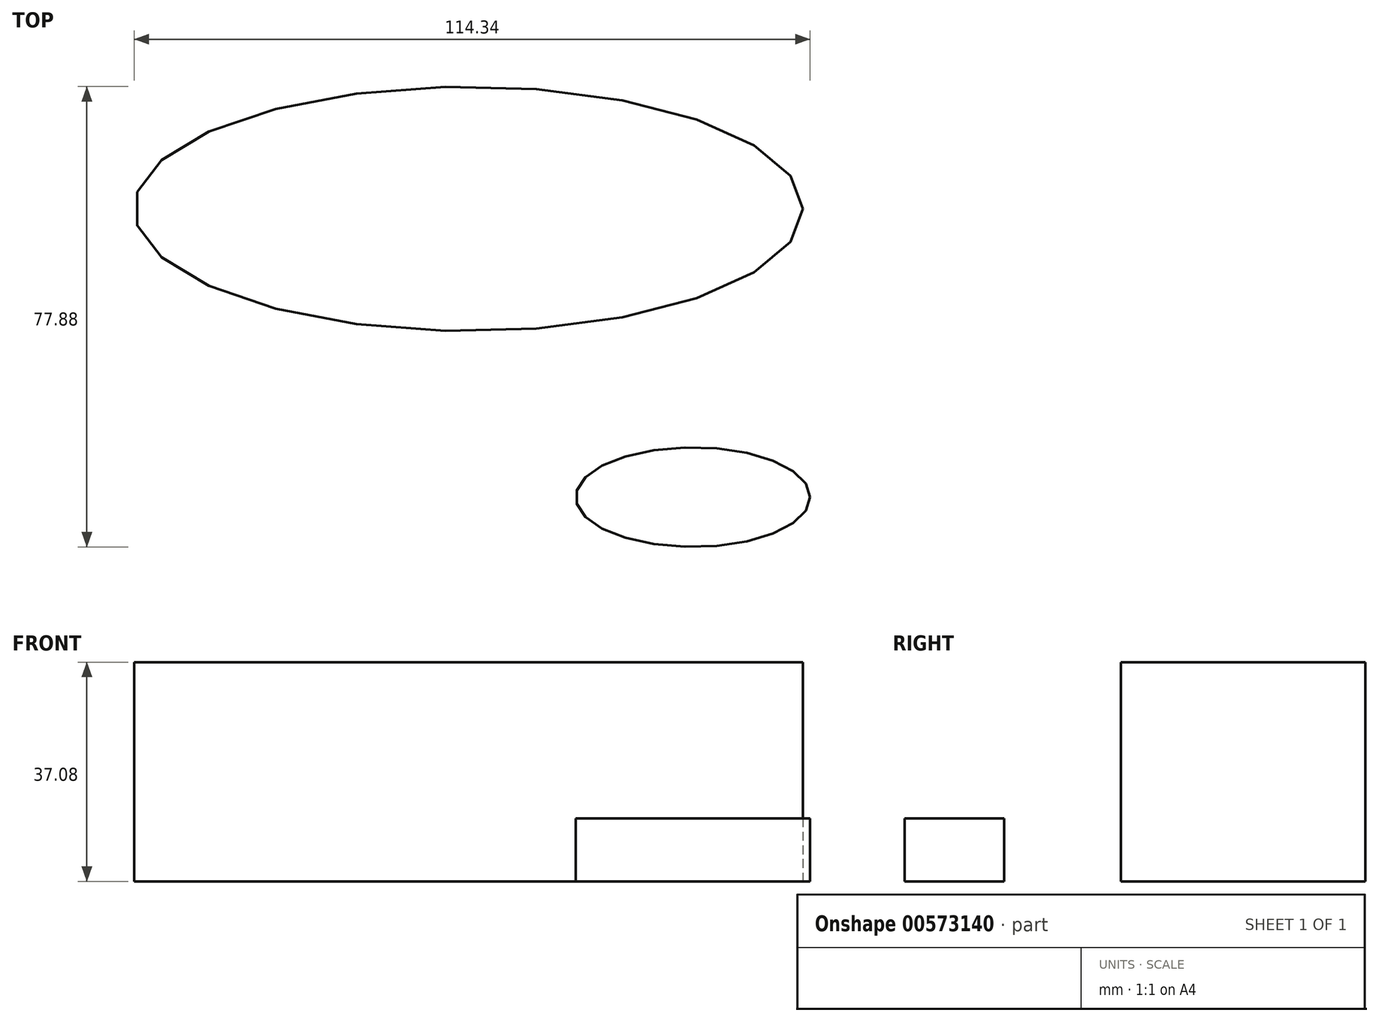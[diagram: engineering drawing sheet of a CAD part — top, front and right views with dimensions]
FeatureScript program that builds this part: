
annotation { "Feature Type Name" : "Feature", "Feature Type Description" : "" }
export const myFeature = defineFeature(function(context is Context, id is Id, definition is map)
    precondition{}
    {
        {
            var Q0;
            Q0=qCreatedBy(makeId("Top.planeOp"),FACE);
            var sketch = newSketch(context, id + "F0", { "sketchPlane" : qUnion([Q0])});
            skEllipse(sketch, "E0", {"center": v(-7.29, 11.51) * mm, "majorRadius": 56.55 * mm, "minorRadius": 20.67 * mm, "majorAxis": v(1, 0)});
            skSolve(sketch);
        }
        {
            var Q0;
            Q0 = qSketchRegion(id + "F0", true);
            extrude(context, id + "F1", {"entities" : qUnion([Q0]), "depth" : 37.08 * mm, "offsetDistance" : 25.4 * mm});
        }
        {
            var Q0;
            Q0=qCreatedBy(makeId("Top.planeOp"),FACE);
            var sketch = newSketch(context, id + "F2", { "sketchPlane" : qUnion([Q0])});
            skEllipse(sketch, "E1", {"center": v(30.68, -37.27) * mm, "majorRadius": 19.83 * mm, "minorRadius": 8.42 * mm, "majorAxis": v(1, 0)});
            skSolve(sketch);
        }
        {
            var Q0;
            Q0 = qSketchRegion(id + "F2", true);
            extrude(context, id + "F3", {"entities" : qUnion([Q0]), "depth" : 10.67 * mm, "offsetDistance" : 25.4 * mm});
        }
    });
